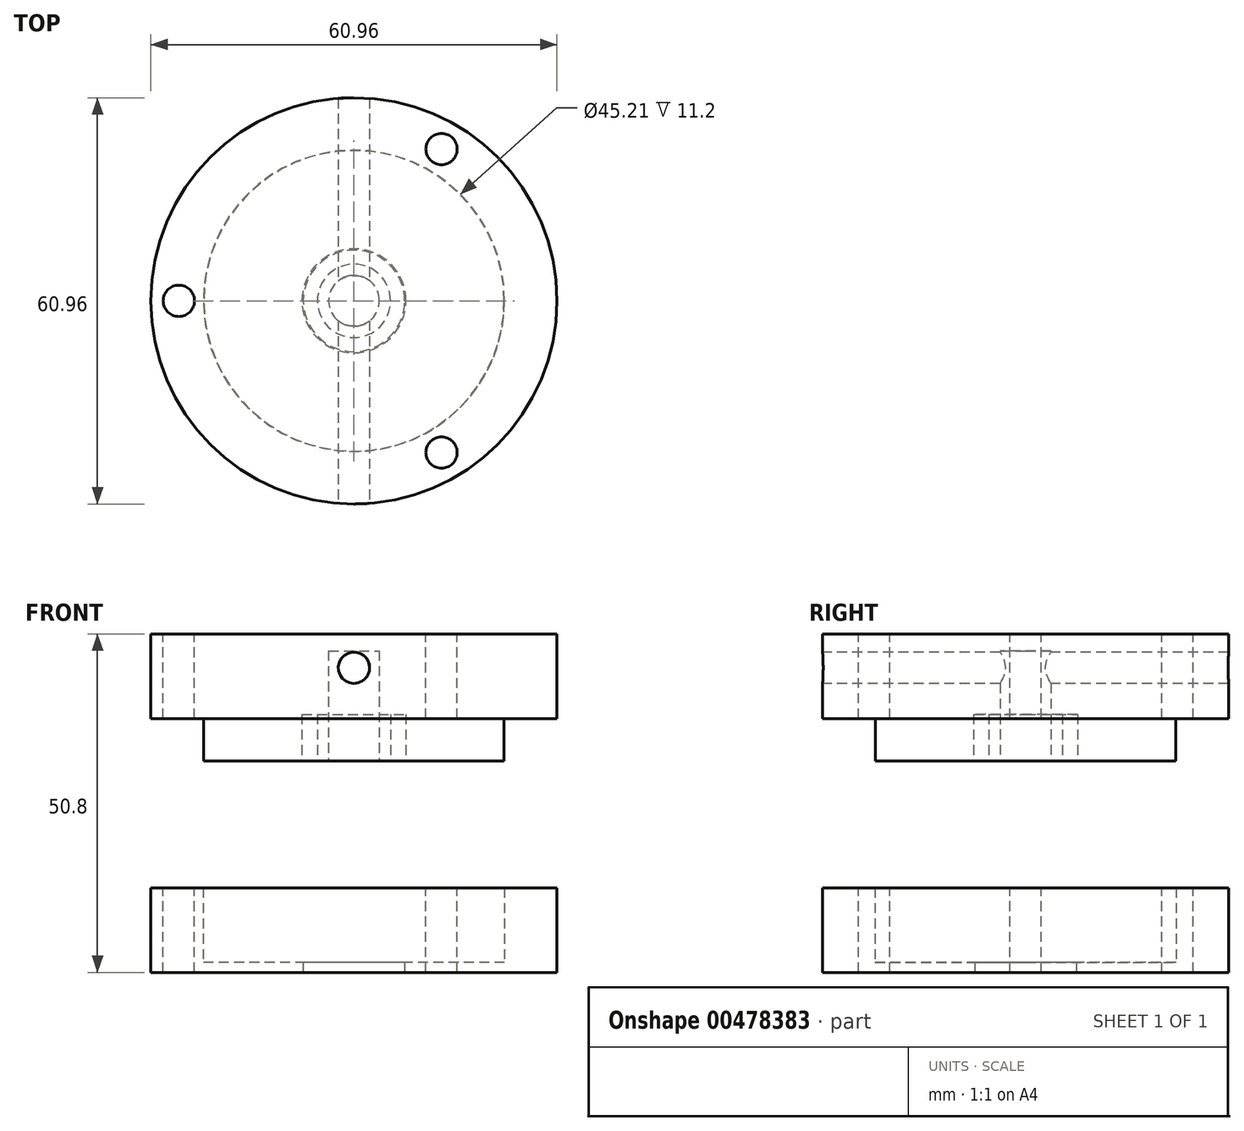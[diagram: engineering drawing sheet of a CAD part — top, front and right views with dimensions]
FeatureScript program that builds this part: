
annotation { "Feature Type Name" : "Feature", "Feature Type Description" : "" }
export const myFeature = defineFeature(function(context is Context, id is Id, definition is map)
    precondition{}
    {
        {
            var Q0;
            Q0=qCreatedBy(makeId("Top.planeOp"),FACE);
            var sketch = newSketch(context, id + "F0", { "sketchPlane" : qUnion([Q0])});
            skCircle(sketch, "E0", {"center": v(0, 0) * mm, "radius": 30.48 * mm});
            skCircle(sketch, "E1", {"center": v(0, 0) * mm, "radius": 22.6 * mm});
            skCircle(sketch, "E2", {"center": v(0, 0) * mm, "radius": 7.62 * mm});
            skSolve(sketch);
        }
        {
            var Q0;
            Q0=makeQuery(id+"F0.imprint","IMPRINT",FACE,{"disambiguationData":[TD([[makeQuery(id+"F0.imprint","IMPRINT",EDGE,{"derivedFrom":sQuery(id+"F0.wireOp",EDGE,"E1")}),1.0]])]});
            extrude(context, id + "F1", {"entities" : qUnion([Q0]), "depth" : 1.5 * mm, "offsetDistance" : 25 * mm});
        }
        {
            var Q0;
            Q0=makeQuery(id+"F0.imprint","IMPRINT",FACE,{"disambiguationData":[TD([[makeQuery(id+"F0.imprint","IMPRINT",EDGE,{"derivedFrom":sQuery(id+"F0.wireOp",EDGE,"E0")}),1.0]])]});
            extrude(context, id + "F2", {"entities" : qUnion([Q0]), "operationType" : NewBodyOperationType.ADD, "depth" : 12.7 * mm, "offsetDistance" : 25 * mm});
        }
        {
            var Q0;
            Q0=makeQuery(id+"F2.opExtrude","CAP_FACE",FACE,{"disambiguationData":[OSD([sQuery(id+"F0.wireOp",EDGE,"E0"),sQuery(id+"F0.wireOp",EDGE,"E1")])],"isStart":false});
            var sketch = newSketch(context, id + "F3", { "sketchPlane" : qUnion([Q0])});
            skLineSegment(sketch, "E3", {"start": v(-30.48, 0) * mm, "end": v(0, 0) * mm, "construction": true});
            skLineSegment(sketch, "E4", {"start": v(0, 0) * mm, "end": v(15.24, 26.4) * mm, "construction": true});
            skLineSegment(sketch, "E5", {"start": v(0, 0) * mm, "end": v(15.24, -26.4) * mm, "construction": true});
            skCircle(sketch, "E6", {"center": v(-26.29, 0) * mm, "radius": 2.35 * mm});
            skCircle(sketch, "E7", {"center": v(13.14, 22.77) * mm, "radius": 2.35 * mm});
            skCircle(sketch, "E8", {"center": v(13.14, -22.77) * mm, "radius": 2.35 * mm});
            skCircle(sketch, "E9", {"center": v(0, 0) * mm, "radius": 26.29 * mm, "construction": true});
            skSolve(sketch);
        }
        {
            var Q0;
            Q0 = qSketchRegion(id + "F3", true);
            var Q1;
            {var subQ0=sQuery(id+"F0.wireOp",EDGE,"E1");Q1=makeQuery(id+"F2.boolean.opBoolean","MERGE",FACE,{"derivedFrom":[makeQuery(id+"F1.opExtrude","CAP_FACE",FACE,{"disambiguationData":[OSD([subQ0,sQuery(id+"F0.wireOp",EDGE,"E2")])],"isStart":true}),makeQuery(id+"F2.opExtrude","CAP_FACE",FACE,{"disambiguationData":[OSD([sQuery(id+"F0.wireOp",EDGE,"E0"),subQ0])],"isStart":true})]});}
            extrude(context, id + "F4", {"entities" : qUnion([Q0]), "operationType" : NewBodyOperationType.REMOVE, "endBound" : BoundingType.UP_TO_SURFACE, "oppositeDirection" : true, "depth" : 25.4 * mm, "endBoundEntityFace" : qUnion([Q1]), "offsetDistance" : 25.4 * mm});
        }
        {
            var Q0;
            Q0=makeQuery(id+"F2.opExtrude","CAP_FACE",FACE,{"disambiguationData":[OSD([sQuery(id+"F0.wireOp",EDGE,"E0"),sQuery(id+"F0.wireOp",EDGE,"E1")])],"isStart":false});
            cPlane(context, id + "F5", {"entities" : qUnion([Q0]), "cplaneType" : CPlaneType.OFFSET, "offset" : 25.4 * mm, "width" : 152.4 * mm, "height" : 152.4 * mm});
        }
        {
            var Q0;
            Q0=qCreatedBy(id+"F5.planeOp",FACE);
            var sketch = newSketch(context, id + "F6", { "sketchPlane" : qUnion([Q0])});
            skCircle(sketch, "E10", {"center": v(0, 0) * mm, "radius": 22.54 * mm});
            skCircle(sketch, "E11", {"center": v(0, 0) * mm, "radius": 30.48 * mm});
            skSolve(sketch);
        }
        {
            var Q0;
            Q0=makeQuery(id+"F6.imprint","IMPRINT",FACE,{"disambiguationData":[TD([[makeQuery(id+"F6.imprint","IMPRINT",EDGE,{"derivedFrom":sQuery(id+"F6.wireOp",EDGE,"E10")}),1.0]])]});
            extrude(context, id + "F7", {"entities" : qUnion([Q0]), "oppositeDirection" : true, "depth" : 6.35 * mm, "offsetDistance" : 25.4 * mm});
        }
        {
            var Q0;
            Q0=makeQuery(id+"F6.imprint","IMPRINT",FACE,{"disambiguationData":[TD([[makeQuery(id+"F6.imprint","IMPRINT",EDGE,{"derivedFrom":sQuery(id+"F6.wireOp",EDGE,"E10")}),1.0]])]});
            var Q1;
            Q1=makeQuery(id+"F6.imprint","IMPRINT",FACE,{"disambiguationData":[TD([[makeQuery(id+"F6.imprint","IMPRINT",EDGE,{"derivedFrom":sQuery(id+"F6.wireOp",EDGE,"E10")}),-1.0]])]});
            extrude(context, id + "F8", {"entities" : qUnion([Q0, Q1]), "operationType" : NewBodyOperationType.ADD, "depth" : 12.7 * mm, "offsetDistance" : 25.4 * mm});
        }
        {
            var Q0;
            Q0=makeQuery(id+"F8.opExtrude","CAP_FACE",FACE,{"disambiguationData":[OSD([sQuery(id+"F6.wireOp",EDGE,"E11")])],"isStart":false});
            var sketch = newSketch(context, id + "F9", { "sketchPlane" : qUnion([Q0])});
            skLineSegment(sketch, "E12", {"start": v(0, 0) * mm, "end": v(-30.48, 0) * mm, "construction": true});
            skLineSegment(sketch, "E13", {"start": v(30.48, 0) * mm, "end": v(0, 0) * mm, "construction": true});
            skLineSegment(sketch, "E14", {"start": v(0, 0) * mm, "end": v(15.24, 26.4) * mm, "construction": true});
            skCircle(sketch, "E15", {"center": v(-26.29, 0) * mm, "radius": 2.35 * mm});
            skCircle(sketch, "E16", {"center": v(13.14, 22.77) * mm, "radius": 2.35 * mm});
            skCircle(sketch, "E17", {"center": v(0, 0) * mm, "radius": 26.29 * mm, "construction": true});
            skLineSegment(sketch, "E18", {"start": v(0, 0) * mm, "end": v(15.24, -26.4) * mm, "construction": true});
            skCircle(sketch, "E19", {"center": v(13.14, -22.77) * mm, "radius": 2.35 * mm});
            skSolve(sketch);
        }
        {
            var Q0;
            Q0=makeQuery(id+"F9.imprint","IMPRINT",FACE,{"disambiguationData":[TD([[makeQuery(id+"F9.imprint","IMPRINT",EDGE,{"derivedFrom":sQuery(id+"F9.wireOp",EDGE,"E16")}),1.0]])]});
            var Q1;
            Q1=makeQuery(id+"F9.imprint","IMPRINT",FACE,{"disambiguationData":[TD([[makeQuery(id+"F9.imprint","IMPRINT",EDGE,{"derivedFrom":sQuery(id+"F9.wireOp",EDGE,"E15")}),1.0]])]});
            var Q2;
            Q2=makeQuery(id+"F9.imprint","IMPRINT",FACE,{"disambiguationData":[TD([[makeQuery(id+"F9.imprint","IMPRINT",EDGE,{"derivedFrom":sQuery(id+"F9.wireOp",EDGE,"E19")}),1.0]])]});
            var Q3;
            Q3=makeQuery(id+"F8.opExtrude","CAP_FACE",FACE,{"disambiguationData":[OSD([sQuery(id+"F6.wireOp",EDGE,"E11")])],"isStart":true});
            extrude(context, id + "F10", {"entities" : qUnion([Q0, Q1, Q2]), "operationType" : NewBodyOperationType.REMOVE, "endBound" : BoundingType.UP_TO_SURFACE, "oppositeDirection" : true, "depth" : 25.4 * mm, "endBoundEntityFace" : qUnion([Q3]), "offsetDistance" : 25.4 * mm});
        }
        {
            var Q0;
            Q0=makeQuery(id+"F7.opExtrude","CAP_FACE",FACE,{"disambiguationData":[OSD([sQuery(id+"F6.wireOp",EDGE,"E10")])],"isStart":false});
            var sketch = newSketch(context, id + "F11", { "sketchPlane" : qUnion([Q0])});
            skCircle(sketch, "E20", {"center": v(0, 0) * mm, "radius": 7.81 * mm});
            skCircle(sketch, "E21", {"center": v(0, 0) * mm, "radius": 5.5 * mm});
            skCircle(sketch, "E22", {"center": v(0, 0) * mm, "radius": 3.81 * mm});
            skSolve(sketch);
        }
        {
            var Q0;
            Q0=makeQuery(id+"F11.imprint","IMPRINT",FACE,{"disambiguationData":[TD([[makeQuery(id+"F11.imprint","IMPRINT",EDGE,{"derivedFrom":sQuery(id+"F11.wireOp",EDGE,"E20")}),1.0]])]});
            extrude(context, id + "F12", {"entities" : qUnion([Q0]), "operationType" : NewBodyOperationType.REMOVE, "oppositeDirection" : true, "depth" : 7 * mm, "offsetDistance" : 25.4 * mm});
        }
        {
            var Q0;
            Q0=makeQuery(id+"F11.imprint","IMPRINT",FACE,{"disambiguationData":[TD([[makeQuery(id+"F11.imprint","IMPRINT",EDGE,{"derivedFrom":sQuery(id+"F11.wireOp",EDGE,"E22")}),1.0]])]});
            extrude(context, id + "F13", {"entities" : qUnion([Q0]), "operationType" : NewBodyOperationType.REMOVE, "oppositeDirection" : true, "depth" : 16.5 * mm, "offsetDistance" : 25.4 * mm});
        }
        {
            var Q0;
            Q0=qCreatedBy(makeId("Front.planeOp"),FACE);
            cPlane(context, id + "F14", {"entities" : qUnion([Q0]), "cplaneType" : CPlaneType.OFFSET, "offset" : 38.1 * mm, "width" : 152.4 * mm, "height" : 152.4 * mm});
        }
        {
            var Q0;
            Q0=qCreatedBy(id+"F14.planeOp",FACE);
            var sketch = newSketch(context, id + "F15", { "sketchPlane" : qUnion([Q0])});
            skCircle(sketch, "E23", {"center": v(0, 45.72) * mm, "radius": 2.35 * mm});
            skSolve(sketch);
        }
        {
            var Q0;
            Q0 = qSketchRegion(id + "F15", true);
            extrude(context, id + "F16", {"entities" : qUnion([Q0]), "operationType" : NewBodyOperationType.REMOVE, "endBound" : BoundingType.THROUGH_ALL, "oppositeDirection" : true, "depth" : 25.4 * mm, "offsetDistance" : 25.4 * mm});
        }
    });
